# Revit family: 120908-00176
name_source: partatom
category: Обобщенные модели
units: mm (PartAtom-declared; Revit-internal decimal feet)

## family parameters
Всегда вертикально = Да
Может служить основой для арматурных стержней = Нет
На основе рабочей плоскости = Нет
Общий = Нет
При загрузке вырезать с полостями = Нет
Размер круглого соединителя = Использовать диаметр
Тип детали = Нормальный
Точка расчета площади = Нет

## types (1)
- Шкаф распределительный телефонный настенный ШРН-В/450(пустой) ССД
    ADSK_Высота = 113 мм
    ADSK_Длина = 500 мм
    ADSK_Изготовитель = АО "СВЯЗЬСТРОЙДЕТАЛЬ"
    ADSK_Код изделия = 120908-00176
    ADSK_Кол-во вводимых кабелей = не более 8
    ADSK_Макс. диаметр вводимого кабеля, мм = не более 32
    ADSK_Марка = Шкафы распределительные настенные ШРН
    ADSK_Масса = 12,8
    ADSK_Наименование = Шкаф распределительный телефонный настенный ШРН-В/450(пустой) ССД
    ADSK_Ссылка на сайт = https://www.ssd.ru
    ADSK_Ширина = 650 мм
    Отметка по умолчанию = 0 мм
